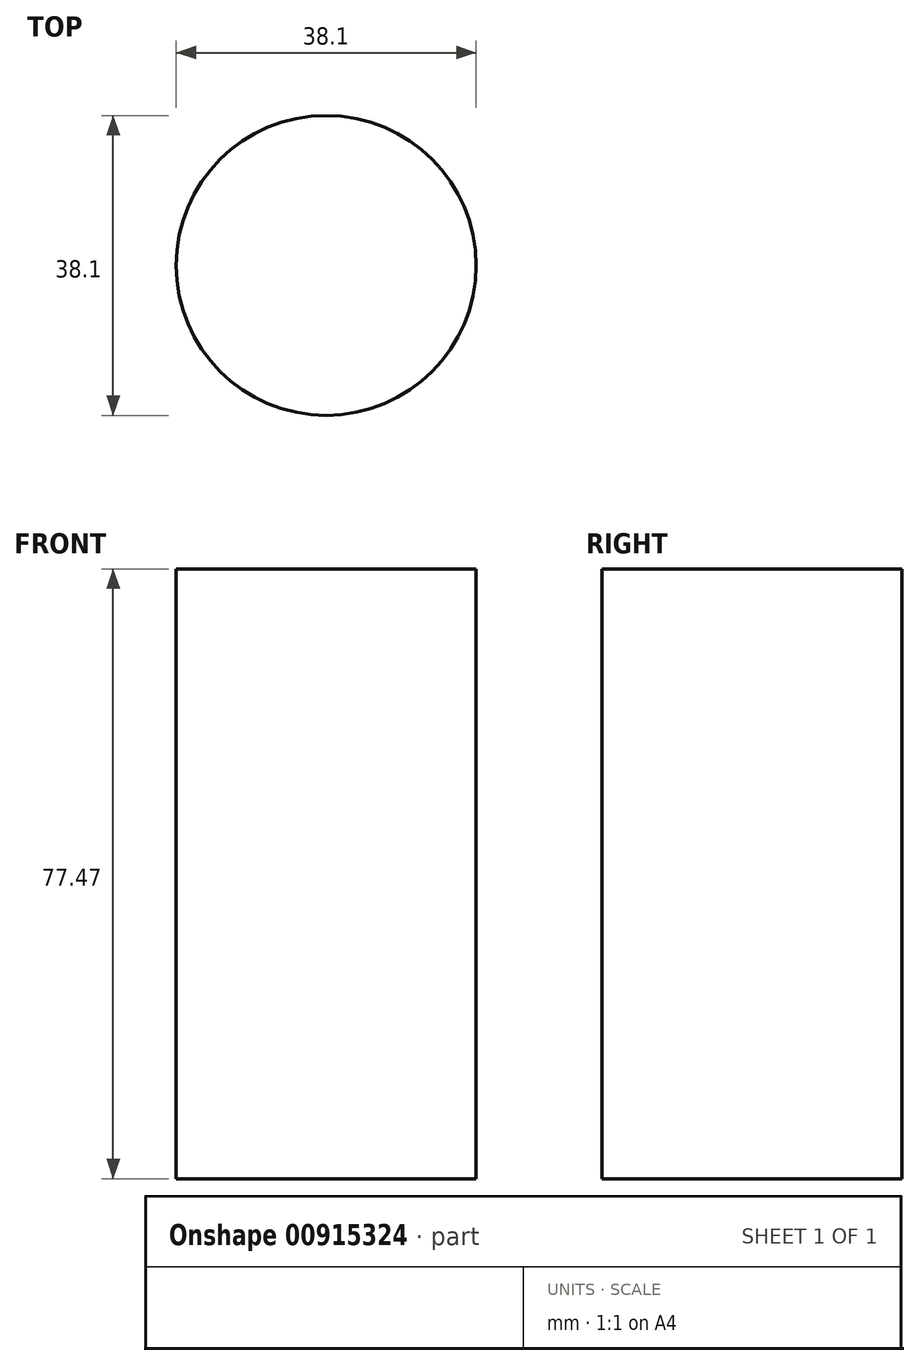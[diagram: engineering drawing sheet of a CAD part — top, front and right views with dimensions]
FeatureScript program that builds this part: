
annotation { "Feature Type Name" : "Feature", "Feature Type Description" : "" }
export const myFeature = defineFeature(function(context is Context, id is Id, definition is map)
    precondition{}
    {
        {
            var Q0;
            Q0=qCreatedBy(makeId("Top.planeOp"),FACE);
            var sketch = newSketch(context, id + "F0", { "sketchPlane" : qUnion([Q0])});
            skCircle(sketch, "E0", {"center": v(0, 0) * mm, "radius": 19.05 * mm});
            skSolve(sketch);
        }
        {
            var Q0;
            Q0=makeQuery(id+"F0.imprint","IMPRINT",FACE,{"disambiguationData":[TD([[makeQuery(id+"F0.imprint","IMPRINT",EDGE,{"derivedFrom":sQuery(id+"F0.wireOp",EDGE,"E0")}),1.0]])]});
            extrude(context, id + "F1", {"entities" : qUnion([Q0]), "depth" : 77.47 * mm, "offsetDistance" : 25.4 * mm});
        }
        {
            var Q0;
            Q0=qCreatedBy(makeId("Right.planeOp"),FACE);
            cPlane(context, id + "F2", {"entities" : qUnion([Q0]), "cplaneType" : CPlaneType.OFFSET, "offset" : 25.4 * mm, "width" : 152.4 * mm, "height" : 152.4 * mm});
        }
    });
